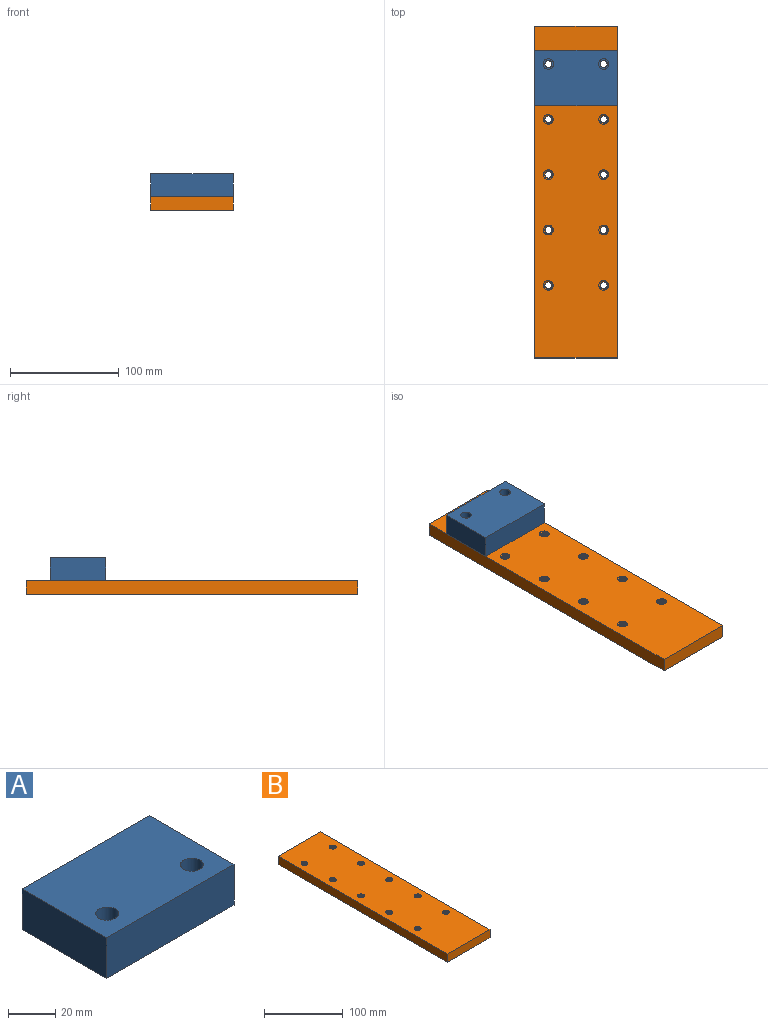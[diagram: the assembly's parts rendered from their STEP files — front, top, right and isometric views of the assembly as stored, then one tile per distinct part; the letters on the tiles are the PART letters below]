
ASSEMBLY  parts=2 mates=1
PART A: 12 faces, bbox 76.2x50.8x21.1 mm
  f0: plane 76.2x21.08mm, normal (0,1,0), area 1606.4mm2, adj f1,f5,f6,f7
  f1: plane 50.8x21.08mm, normal (-1,0,0), area 1071mm2, adj f0,f2,f6,f7
  f2: plane 76.2x21.08mm, normal (0,-1,0), area 1606.4mm2, adj f1,f5,f6,f7
  f3: cylinder r=4.84mm len=9.68mm, axis (0,0,-1), area 204.6mm2, adj f6,f9
  f4: cylinder r=4.84mm len=9.68mm, axis (0,0,-1), area 204.6mm2, adj f6,f11
  f5: plane 50.8x21.08mm, normal (1,0,0), area 1071mm2, adj f0,f2,f6,f7
  f6: plane 76.2x50.8mm, normal (0,0,1), area 3723.9mm2, adj f0,f1,f2,f3,f4,f5
  f7: plane 76.2x50.8mm, normal (0,0,-1), area 3804mm2, adj f0,f1,f2,f5,f8,f10
  f8: cylinder r=3.26mm len=14.35mm, axis (0,0,-1), area 294.3mm2, adj f7,f9
  f9: plane 9.68x9.68mm, normal (0,0,1), area 40.1mm2, adj f3,f8
  f10: cylinder r=3.26mm len=14.35mm, axis (0,0,-1), area 294.3mm2, adj f7,f11
  f11: plane 9.68x9.68mm, normal (0,0,1), area 40.1mm2, adj f4,f10
PART B: 56 faces, bbox 76.9x305.5x14.4 mm
  f0: plane 76.2x12.7mm, normal (0,1,0), area 967.7mm2, adj f1,f13,f14,f15
  f1: plane 304.8x12.7mm, normal (-1,0,0), area 3871mm2, adj f0,f2,f14,f15
  f2: plane 76.2x12.7mm, normal (0,-1,0), area 967.7mm2, adj f1,f13,f14,f15
  f3: cylinder r=3.17mm len=11.43mm, axis (0,0,-1), area 5.8mm2, adj f15,f21,f22,f23
  f4: cylinder r=3.17mm len=11.43mm, axis (0,0,-1), area 5.8mm2, adj f15,f33,f34,f35
  f5: cylinder r=3.17mm len=11.43mm, axis (0,0,-1), area 5.8mm2, adj f15,f37,f38,f39
  f6: cylinder r=3.17mm len=11.43mm, axis (0,0,-1), area 5.8mm2, adj f15,f40,f41,f43
  f7: cylinder r=3.17mm len=11.43mm, axis (0,0,-1), area 5.8mm2, adj f15,f49,f52,f53
  f8: cylinder r=3.17mm len=11.43mm, axis (0,0,-1), area 5.8mm2, adj f15,f25,f26,f27
  f9: cylinder r=3.17mm len=11.43mm, axis (0,0,-1), area 5.8mm2, adj f15,f28,f29,f31
  f10: cylinder r=3.17mm len=11.43mm, axis (0,0,-1), area 5.8mm2, adj f15,f17,f18,f19
  f11: cylinder r=3.17mm len=11.43mm, axis (0,0,-1), area 5.8mm2, adj f15,f45,f50,f51
  f12: cylinder r=3.17mm len=11.43mm, axis (0,0,-1), area 5.8mm2, adj f15,f47,f54,f55
  f13: plane 304.8x12.7mm, normal (1,0,0), area 3871mm2, adj f0,f2,f14,f15
  f14: plane 304.8x76.2mm, normal (0,0,1), area 22605mm2, adj f0,f1,f2,f13,f16,f20,f24,f30
  f15: plane 305.54x76.94mm, normal (0,0,-1), area 22810.8mm2, adj f0,f1,f2,f3,f4,f5,f6,f7
  f16: cone r=3.17mm half-angle=45deg, axis (0,0,1), area 28.7mm2, adj f14,f17,f18,f19
  f17: cone r=3.17mm half-angle=45deg, axis (0,0,1), area 0.4mm2, adj f10,f16,f19
  f18: bspline ~13.56x8.33mm, area 247.4mm2, adj f10,f15,f16,f19
  f19: bspline ~13.27x9.62mm, area 248.2mm2, adj f10,f15,f16,f17,f18
  f20: cone r=3.17mm half-angle=45deg, axis (0,0,1), area 28.7mm2, adj f14,f21,f22,f23
  f21: cone r=3.17mm half-angle=45deg, axis (0,0,1), area 0.4mm2, adj f3,f20,f23
  f22: bspline ~13.56x8.33mm, area 247.4mm2, adj f3,f15,f20,f23
  f23: bspline ~13.27x9.62mm, area 248.2mm2, adj f3,f15,f20,f21,f22
  f24: cone r=3.17mm half-angle=45deg, axis (0,0,1), area 28.7mm2, adj f14,f25,f26,f27
  f25: cone r=3.17mm half-angle=45deg, axis (0,0,1), area 0.4mm2, adj f8,f24,f27
  f26: bspline ~13.56x8.33mm, area 247.4mm2, adj f8,f15,f24,f27
  f27: bspline ~13.27x9.62mm, area 248.2mm2, adj f8,f15,f24,f25,f26
  f28: bspline ~13.56x8.33mm, area 247.4mm2, adj f9,f15,f29,f30
  f29: bspline ~13.27x9.62mm, area 248.2mm2, adj f9,f15,f28,f30,f31
  f30: cone r=3.17mm half-angle=45deg, axis (0,0,1), area 28.7mm2, adj f14,f28,f29,f31
  f31: cone r=3.17mm half-angle=45deg, axis (0,0,1), area 0.4mm2, adj f9,f29,f30
  f32: cone r=3.17mm half-angle=45deg, axis (0,0,1), area 28.7mm2, adj f14,f33,f34,f35
  f33: cone r=3.17mm half-angle=45deg, axis (0,0,1), area 0.4mm2, adj f4,f32,f35
  f34: bspline ~13.56x8.33mm, area 247.4mm2, adj f4,f15,f32,f35
  f35: bspline ~13.27x9.62mm, area 248.2mm2, adj f4,f15,f32,f33,f34
  f36: cone r=3.17mm half-angle=45deg, axis (0,0,1), area 28.7mm2, adj f14,f37,f38,f39
  f37: cone r=3.17mm half-angle=45deg, axis (0,0,1), area 0.4mm2, adj f5,f36,f39
  f38: bspline ~13.56x8.33mm, area 247.4mm2, adj f5,f15,f36,f39
  f39: bspline ~13.27x9.62mm, area 248.2mm2, adj f5,f15,f36,f37,f38
  f40: bspline ~13.56x8.33mm, area 247.4mm2, adj f6,f15,f41,f42
  f41: bspline ~13.27x9.62mm, area 248.2mm2, adj f6,f15,f40,f42,f43
  f42: cone r=3.17mm half-angle=45deg, axis (0,0,1), area 28.7mm2, adj f14,f40,f41,f43
  f43: cone r=3.17mm half-angle=45deg, axis (0,0,1), area 0.4mm2, adj f6,f41,f42
  f44: cone r=3.17mm half-angle=45deg, axis (0,0,1), area 28.7mm2, adj f14,f45,f50,f51
  f45: cone r=3.17mm half-angle=45deg, axis (0,0,1), area 0.4mm2, adj f11,f44,f51
  f46: cone r=3.17mm half-angle=45deg, axis (0,0,1), area 28.7mm2, adj f14,f47,f54,f55
  f47: cone r=3.17mm half-angle=45deg, axis (0,0,1), area 0.4mm2, adj f12,f46,f55
  f48: cone r=3.17mm half-angle=45deg, axis (0,0,1), area 28.7mm2, adj f14,f49,f52,f53
  f49: cone r=3.17mm half-angle=45deg, axis (0,0,1), area 0.4mm2, adj f7,f48,f53
  f50: bspline ~13.56x8.33mm, area 247.4mm2, adj f11,f15,f44,f51
  f51: bspline ~13.27x9.62mm, area 248.2mm2, adj f11,f15,f44,f45,f50
  f52: bspline ~13.56x8.33mm, area 247.4mm2, adj f7,f15,f48,f53
  f53: bspline ~13.27x9.62mm, area 248.2mm2, adj f7,f15,f48,f49,f52
  f54: bspline ~13.56x8.33mm, area 247.4mm2, adj f12,f15,f46,f55
  f55: bspline ~13.27x9.62mm, area 248.2mm2, adj f12,f15,f46,f47,f54
PLACE A rot(axis=(0,0,1),180deg) t=(-42.61,234.11,12.7)mm
PLACE B at identity
MATE fastened A.f3 <-> B.f7  axis (0,0,-1) through (-17.23,235.28,12.7)mm
